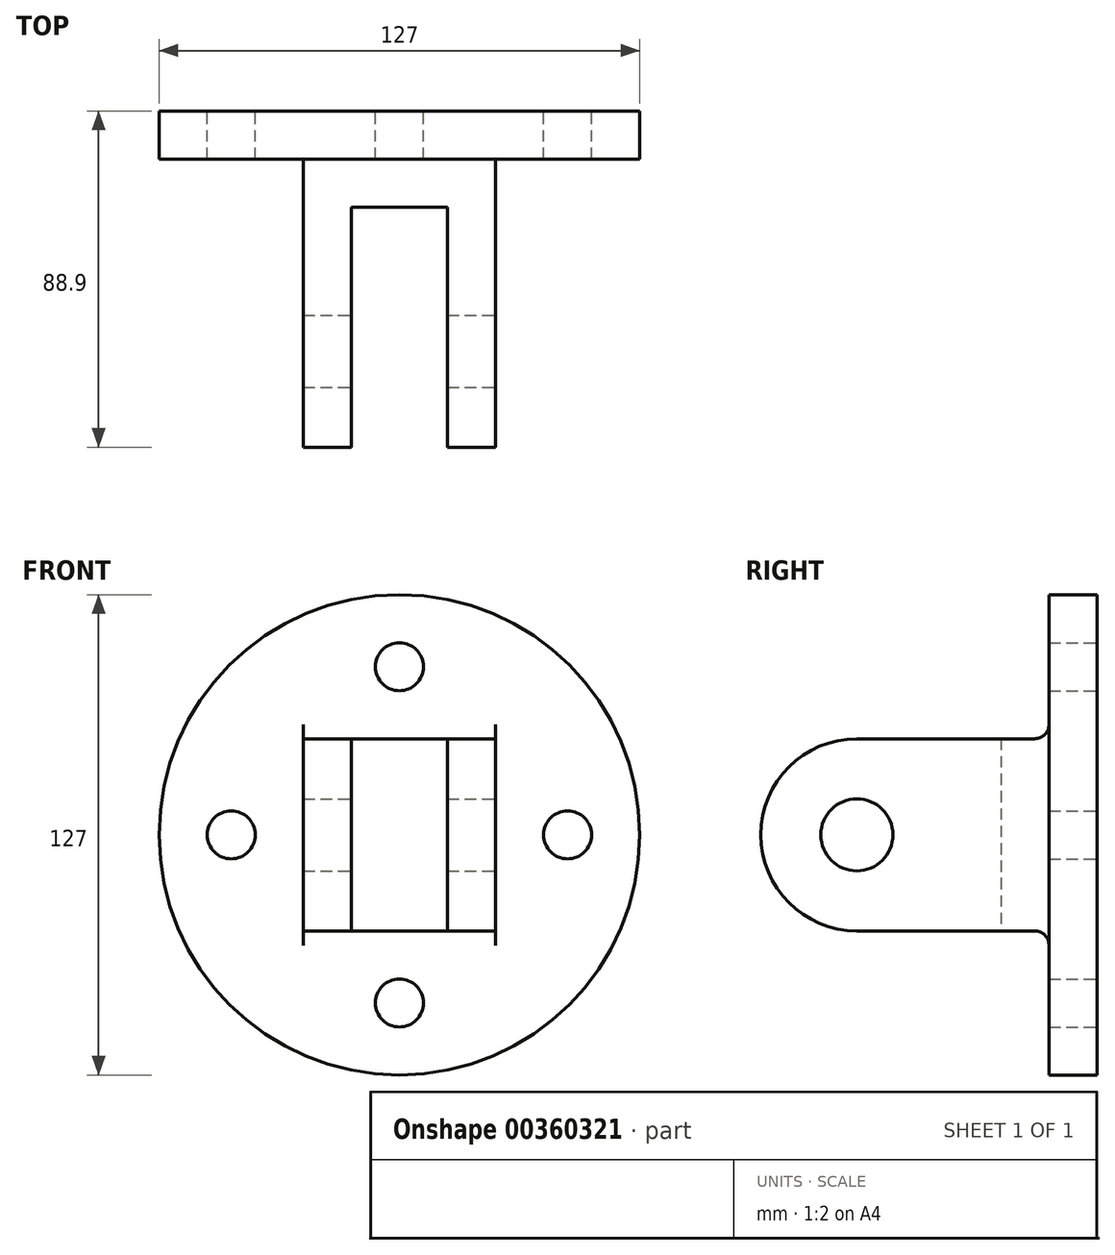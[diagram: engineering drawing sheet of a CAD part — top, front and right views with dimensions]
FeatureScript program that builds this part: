
annotation { "Feature Type Name" : "Feature", "Feature Type Description" : "" }
export const myFeature = defineFeature(function(context is Context, id is Id, definition is map)
    precondition{}
    {
        {
            var Q0;
            Q0=qCreatedBy(makeId("Front.planeOp"),FACE);
            var sketch = newSketch(context, id + "F0", { "sketchPlane" : qUnion([Q0])});
            skCircle(sketch, "E0", {"center": v(0, 0) * mm, "radius": 63.5 * mm});
            skCircle(sketch, "E1", {"center": v(0, 0) * mm, "radius": 44.45 * mm, "construction": true});
            skCircle(sketch, "E2", {"center": v(0, 44.45) * mm, "radius": 6.35 * mm});
            skCircle(sketch, "E3", {"center": v(-44.45, 0) * mm, "radius": 6.35 * mm});
            skCircle(sketch, "E4", {"center": v(44.45, 0) * mm, "radius": 6.35 * mm});
            skCircle(sketch, "E5", {"center": v(0, -44.45) * mm, "radius": 6.35 * mm});
            skLineSegment(sketch, "E6.bottom", {"start": v(-25.4, 25.4) * mm, "end": v(25.4, 25.4) * mm});
            skLineSegment(sketch, "E6.top", {"start": v(-25.4, -25.4) * mm, "end": v(25.4, -25.4) * mm});
            skLineSegment(sketch, "E6.left", {"start": v(-25.4, 25.4) * mm, "end": v(-25.4, -25.4) * mm});
            skLineSegment(sketch, "E6.right", {"start": v(25.4, 25.4) * mm, "end": v(25.4, -25.4) * mm});
            skLineSegment(sketch, "E7", {"start": v(-12.7, 25.4) * mm, "end": v(-12.7, -25.4) * mm});
            skLineSegment(sketch, "E8", {"start": v(12.7, 25.4) * mm, "end": v(12.7, -25.4) * mm});
            skLineSegment(sketch, "E9", {"start": v(0, 25.4) * mm, "end": v(0, -25.4) * mm, "construction": true});
            skSolve(sketch);
        }
        {
            var Q0;
            Q0=makeQuery(id+"F0.imprint","IMPRINT",FACE,{"disambiguationData":[TD([[makeQuery(id+"F0.imprint","IMPRINT",EDGE,{"derivedFrom":sQuery(id+"F0.wireOp",EDGE,"E0")}),1.0]])]});
            extrude(context, id + "F1", {"entities" : qUnion([Q0]), "depth" : 12.7 * mm});
        }
        {
            var Q0;
            {var subQ0=sQuery(id+"F0.wireOp",EDGE,"E6.left");Q0=makeQuery(id+"F0.imprint","IMPRINT",FACE,{"disambiguationData":[TD([[makeQuery(id+"F0.imprint","IMPRINT",EDGE,{"derivedFrom":subQ0}),1.0]])]});}
            var Q1;
            {var subQ0=sQuery(id+"F0.wireOp",EDGE,"E6.right");Q1=makeQuery(id+"F0.imprint","IMPRINT",FACE,{"disambiguationData":[TD([[makeQuery(id+"F0.imprint","IMPRINT",EDGE,{"derivedFrom":subQ0}),-1.0]])]});}
            extrude(context, id + "F2", {"entities" : qUnion([Q0, Q1]), "operationType" : NewBodyOperationType.ADD, "depth" : 127 * mm});
        }
        {
            var Q0;
            {var subQ0=sQuery(id+"F0.wireOp",EDGE,"E7");Q0=makeQuery(id+"F0.imprint","IMPRINT",FACE,{"disambiguationData":[TD([[makeQuery(id+"F0.imprint","IMPRINT",EDGE,{"derivedFrom":subQ0}),1.0]])]});}
            extrude(context, id + "F3", {"entities" : qUnion([Q0]), "operationType" : NewBodyOperationType.ADD, "depth" : 25.4 * mm});
        }
        {
            var Q0;
            Q0=makeQuery(id+"F2.opExtrude","SWEPT_FACE",FACE,{"disambiguationData":[OSD([sQuery(id+"F0.wireOp",EDGE,"E6.right")])]});
            var sketch = newSketch(context, id + "F4", { "sketchPlane" : qUnion([Q0])});
            skLineSegment(sketch, "E10", {"start": v(-12.7, -25.4) * mm, "end": v(-63.5, -25.4) * mm});
            skLineSegment(sketch, "E11", {"start": v(-12.7, 25.4) * mm, "end": v(-63.5, 25.4) * mm});
            skArc(sketch, "E12", {"start": v(-63.5, 25.4) * mm, "mid": v(-88.9, 0) * mm, "end": v(-63.5, -25.4) * mm});
            skCircle(sketch, "E13", {"center": v(-63.5, 0) * mm, "radius": 9.53 * mm});
            skSolve(sketch);
        }
        {
            var Q0;
            {var subQ0=sQuery(id+"F4.wireOp",EDGE,"E12");Q0=makeQuery(id+"F4.imprint","IMPRINT",FACE,{"disambiguationData":[TD([[makeQuery(id+"F4.imprint","IMPRINT",EDGE,{"derivedFrom":subQ0}),-1.0]])]});}
            var Q1;
            Q1=makeQuery(id+"F4.imprint","IMPRINT",FACE,{"disambiguationData":[TD([[makeQuery(id+"F4.imprint","IMPRINT",EDGE,{"derivedFrom":sQuery(id+"F4.wireOp",EDGE,"E13")}),1.0]])]});
            extrude(context, id + "F5", {"entities" : qUnion([Q0, Q1]), "operationType" : NewBodyOperationType.REMOVE, "oppositeDirection" : true, "depth" : 254 * mm});
        }
        {
            var Q0;
            {var subQ0=sQuery(id+"F0.wireOp",EDGE,"E6.right");var subQ1=sQuery(id+"F0.wireOp",EDGE,"E6.left");var subQ2=sQuery(id+"F0.wireOp",EDGE,"E6.bottom");var subQ4=makeQuery(id+"F1.opExtrude","CAP_EDGE",EDGE,{"disambiguationData":[OSD([subQ2])],"isStart":false});Q0=makeQuery(id+"F3.boolean.opBoolean","MERGE",EDGE,{"derivedFrom":[makeQuery(id+"F2.boolean.opBoolean","SPLIT",EDGE,{"disambiguationData":[topologyDisambiguationEdgeConnected([makeQuery(id+"F2.opExtrude","SWEPT_FACE",FACE,{"disambiguationData":[OSD([subQ2]),TDD([makeQuery(id+"F0.imprint","IMPRINT",EDGE,{"disambiguationData":[TD([[makeQuery(id+"F0.imprint","INTERSECT",VERTEX,{"derivedFrom":[subQ2,subQ1]}),-1.0]])],"derivedFrom":subQ2})])]})])],"derivedFrom":subQ4}),makeQuery(id+"F2.boolean.opBoolean","SPLIT",EDGE,{"disambiguationData":[topologyDisambiguationEdgeConnected([makeQuery(id+"F2.opExtrude","SWEPT_FACE",FACE,{"disambiguationData":[OSD([subQ2]),TDD([makeQuery(id+"F0.imprint","IMPRINT",EDGE,{"disambiguationData":[TD([[makeQuery(id+"F0.imprint","INTERSECT",VERTEX,{"derivedFrom":[subQ2,subQ0]}),1.0]])],"derivedFrom":subQ2})])]})])],"derivedFrom":subQ4}),makeQuery(id+"F2.boolean.opBoolean","SPLIT",EDGE,{"disambiguationData":[topologyDisambiguationEdgeConnected([makeQuery(id+"F1.opExtrude","SWEPT_FACE",FACE,{"disambiguationData":[OSD([subQ2])]})])],"derivedFrom":subQ4})]});}
            var Q1;
            Q1=makeQuery(id+"F1.opExtrude","CAP_EDGE",EDGE,{"disambiguationData":[OSD([sQuery(id+"F0.wireOp",EDGE,"E6.right")])],"isStart":false});
            var Q2;
            {var subQ0=sQuery(id+"F0.wireOp",EDGE,"E6.right");var subQ1=sQuery(id+"F0.wireOp",EDGE,"E6.left");var subQ2=sQuery(id+"F0.wireOp",EDGE,"E6.top");var subQ4=makeQuery(id+"F1.opExtrude","CAP_EDGE",EDGE,{"disambiguationData":[OSD([subQ2])],"isStart":false});Q2=makeQuery(id+"F3.boolean.opBoolean","MERGE",EDGE,{"derivedFrom":[makeQuery(id+"F2.boolean.opBoolean","SPLIT",EDGE,{"disambiguationData":[topologyDisambiguationEdgeConnected([makeQuery(id+"F2.opExtrude","SWEPT_FACE",FACE,{"disambiguationData":[OSD([subQ2]),TDD([makeQuery(id+"F0.imprint","IMPRINT",EDGE,{"disambiguationData":[TD([[makeQuery(id+"F0.imprint","INTERSECT",VERTEX,{"derivedFrom":[subQ2,subQ1]}),-1.0]])],"derivedFrom":subQ2})])]})])],"derivedFrom":subQ4}),makeQuery(id+"F2.boolean.opBoolean","SPLIT",EDGE,{"disambiguationData":[topologyDisambiguationEdgeConnected([makeQuery(id+"F2.opExtrude","SWEPT_FACE",FACE,{"disambiguationData":[OSD([subQ2]),TDD([makeQuery(id+"F0.imprint","IMPRINT",EDGE,{"disambiguationData":[TD([[makeQuery(id+"F0.imprint","INTERSECT",VERTEX,{"derivedFrom":[subQ2,subQ0]}),1.0]])],"derivedFrom":subQ2})])]})])],"derivedFrom":subQ4}),makeQuery(id+"F2.boolean.opBoolean","SPLIT",EDGE,{"disambiguationData":[topologyDisambiguationEdgeConnected([makeQuery(id+"F1.opExtrude","SWEPT_FACE",FACE,{"disambiguationData":[OSD([subQ2])]})])],"derivedFrom":subQ4})]});}
            var Q3;
            Q3=makeQuery(id+"F1.opExtrude","CAP_EDGE",EDGE,{"disambiguationData":[OSD([sQuery(id+"F0.wireOp",EDGE,"E6.left")])],"isStart":false});
            fillet(context, id + "F6", {"entities" : qUnion([Q0, Q1, Q2, Q3]), "radius" : 3.8 * mm, "tangentPropagation" : true, "allowEdgeOverflow" : false});
        }
    });
